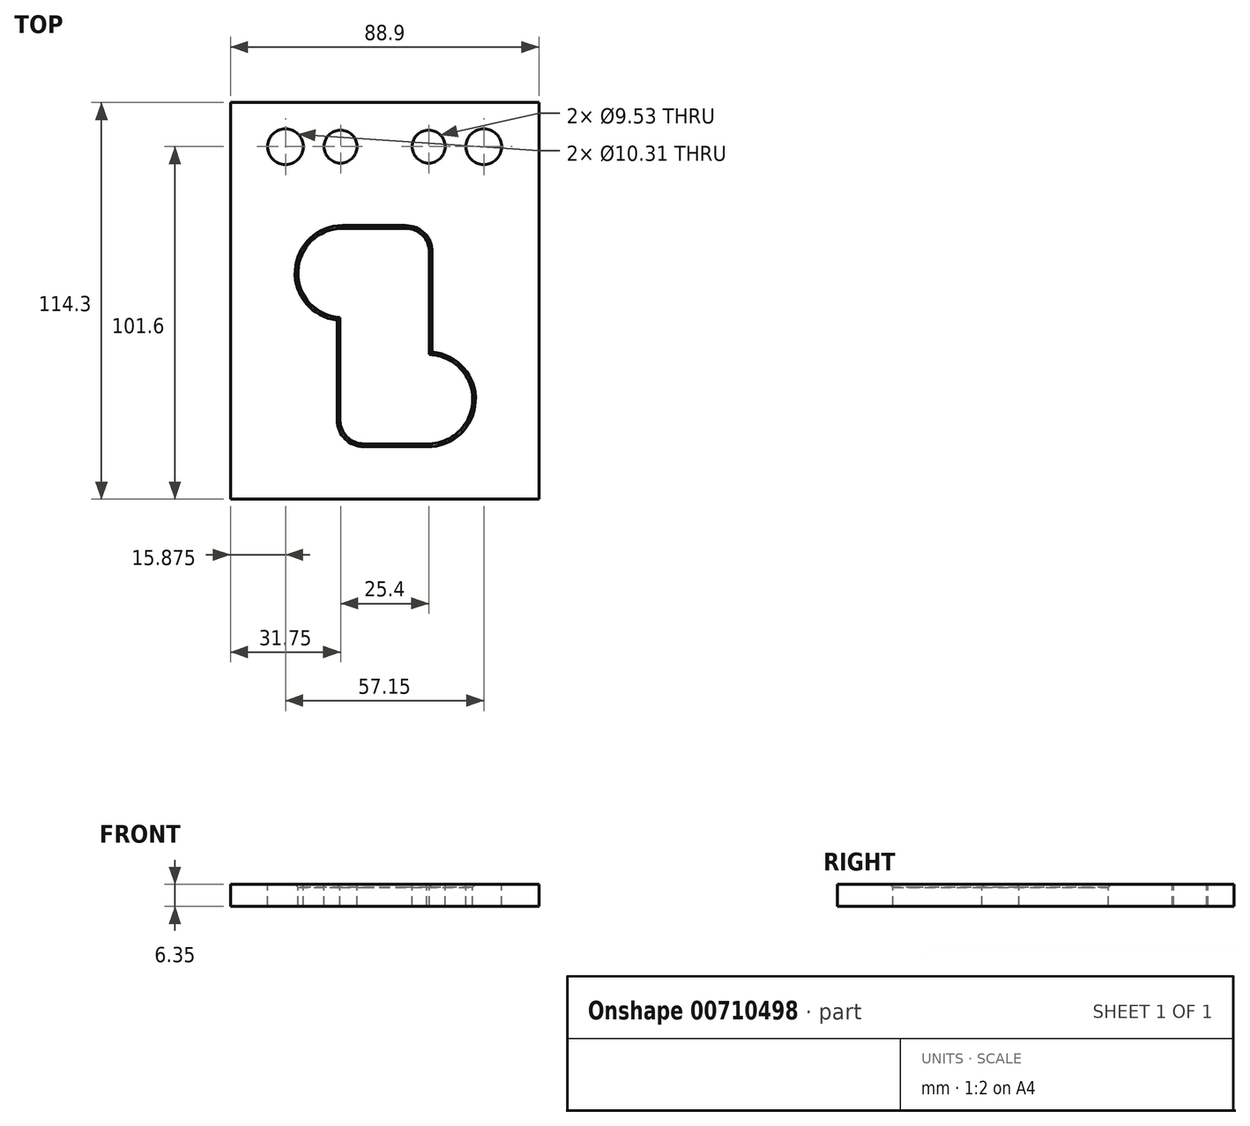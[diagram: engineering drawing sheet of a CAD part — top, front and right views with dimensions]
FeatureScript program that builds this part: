
annotation { "Feature Type Name" : "Feature", "Feature Type Description" : "" }
export const myFeature = defineFeature(function(context is Context, id is Id, definition is map)
    precondition{}
    {
        {
            var Q0;
            Q0=qCreatedBy(makeId("Top.planeOp"),FACE);
            var sketch = newSketch(context, id + "F0", { "sketchPlane" : qUnion([Q0])});
            skLineSegment(sketch, "E0.0", {"start": v(6.06, 20.9) * mm, "end": v(-12.1, 20.9) * mm});
            skArc(sketch, "E0.1", {"start": v(12.87, 14.1) * mm, "mid": v(10.87, 18.9) * mm, "end": v(6.06, 20.9) * mm});
            skArc(sketch, "E0.2", {"start": v(-12.1, 20.9) * mm, "mid": v(-24.97, 8.4) * mm, "end": v(-12.84, -4.81) * mm});
            skLineSegment(sketch, "E0.3", {"start": v(12.87, -15.48) * mm, "end": v(12.87, 14.1) * mm});
            skLineSegment(sketch, "E0.4", {"start": v(-12.84, -34.38) * mm, "end": v(-12.84, -4.81) * mm});
            skArc(sketch, "E0.5", {"start": v(-12.84, -34.38) * mm, "mid": v(-10.84, -39.2) * mm, "end": v(-6.03, -41.2) * mm});
            skLineSegment(sketch, "E0.6", {"start": v(12.14, -41.2) * mm, "end": v(-6.03, -41.2) * mm});
            skArc(sketch, "E0.7", {"start": v(12.14, -41.2) * mm, "mid": v(25.36, -28.7) * mm, "end": v(12.87, -15.48) * mm});
            skLineSegment(sketch, "E1.bottom", {"start": v(44.45, -57.15) * mm, "end": v(-44.45, -57.15) * mm});
            skLineSegment(sketch, "E1.top", {"start": v(44.45, 57.15) * mm, "end": v(-44.45, 57.15) * mm});
            skLineSegment(sketch, "E1.left", {"start": v(44.45, -57.15) * mm, "end": v(44.45, 57.15) * mm});
            skLineSegment(sketch, "E1.right", {"start": v(-44.45, -57.15) * mm, "end": v(-44.45, 57.15) * mm});
            skPoint(sketch, "E1.middle", {"position": v(0, 0) * mm});
            skLineSegment(sketch, "E2", {"start": v(-44.45, 44.45) * mm, "end": v(44.45, 44.45) * mm});
            skLineSegment(sketch, "E3", {"start": v(-28.57, 57.15) * mm, "end": v(-28.57, 44.45) * mm});
            skLineSegment(sketch, "E4", {"start": v(28.57, 57.15) * mm, "end": v(28.57, 44.45) * mm});
            skLineSegment(sketch, "E5", {"start": v(-12.7, 44.45) * mm, "end": v(-12.7, 57.15) * mm});
            skLineSegment(sketch, "E6", {"start": v(12.7, 44.45) * mm, "end": v(12.7, 57.15) * mm});
            skCircle(sketch, "E7", {"center": v(-12.7, 44.45) * mm, "radius": 4.76 * mm});
            skCircle(sketch, "E8", {"center": v(12.7, 44.45) * mm, "radius": 4.76 * mm});
            skCircle(sketch, "E9", {"center": v(-28.57, 44.45) * mm, "radius": 5.16 * mm});
            skCircle(sketch, "E10", {"center": v(28.57, 44.45) * mm, "radius": 5.16 * mm});
            skSolve(sketch);
        }
        {
            var Q0;
            Q0 = qSketchRegion(id + "F0", true);
            extrude(context, id + "F1", {"entities" : qUnion([Q0]), "depth" : -6.35 * mm, "offsetDistance" : 25.4 * mm});
        }
        {
            var Q0;
            Q0=makeQuery(id+"F1.opExtrude","CAP_EDGE",EDGE,{"disambiguationData":[OSD([sQuery(id+"F0.wireOp",EDGE,"E0.3")])],"isStart":true});
            var Q1;
            Q1=makeQuery(id+"F1.opExtrude","CAP_EDGE",EDGE,{"disambiguationData":[OSD([sQuery(id+"F0.wireOp",EDGE,"E0.4")])],"isStart":true});
            var Q2;
            Q2=makeQuery(id+"F1.opExtrude","CAP_EDGE",EDGE,{"disambiguationData":[OSD([sQuery(id+"F0.wireOp",EDGE,"E0.5")])],"isStart":true});
            var Q3;
            Q3=makeQuery(id+"F1.opExtrude","CAP_EDGE",EDGE,{"disambiguationData":[OSD([sQuery(id+"F0.wireOp",EDGE,"E0.6")])],"isStart":true});
            var Q4;
            Q4=makeQuery(id+"F1.opExtrude","CAP_EDGE",EDGE,{"disambiguationData":[OSD([sQuery(id+"F0.wireOp",EDGE,"E0.7")])],"isStart":true});
            chamfer(context, id + "F2", {"entities" : qUnion([Q0, Q1, Q2, Q3, Q4]), "width" : 0.81 * mm, "tangentPropagation" : true});
        }
    });
